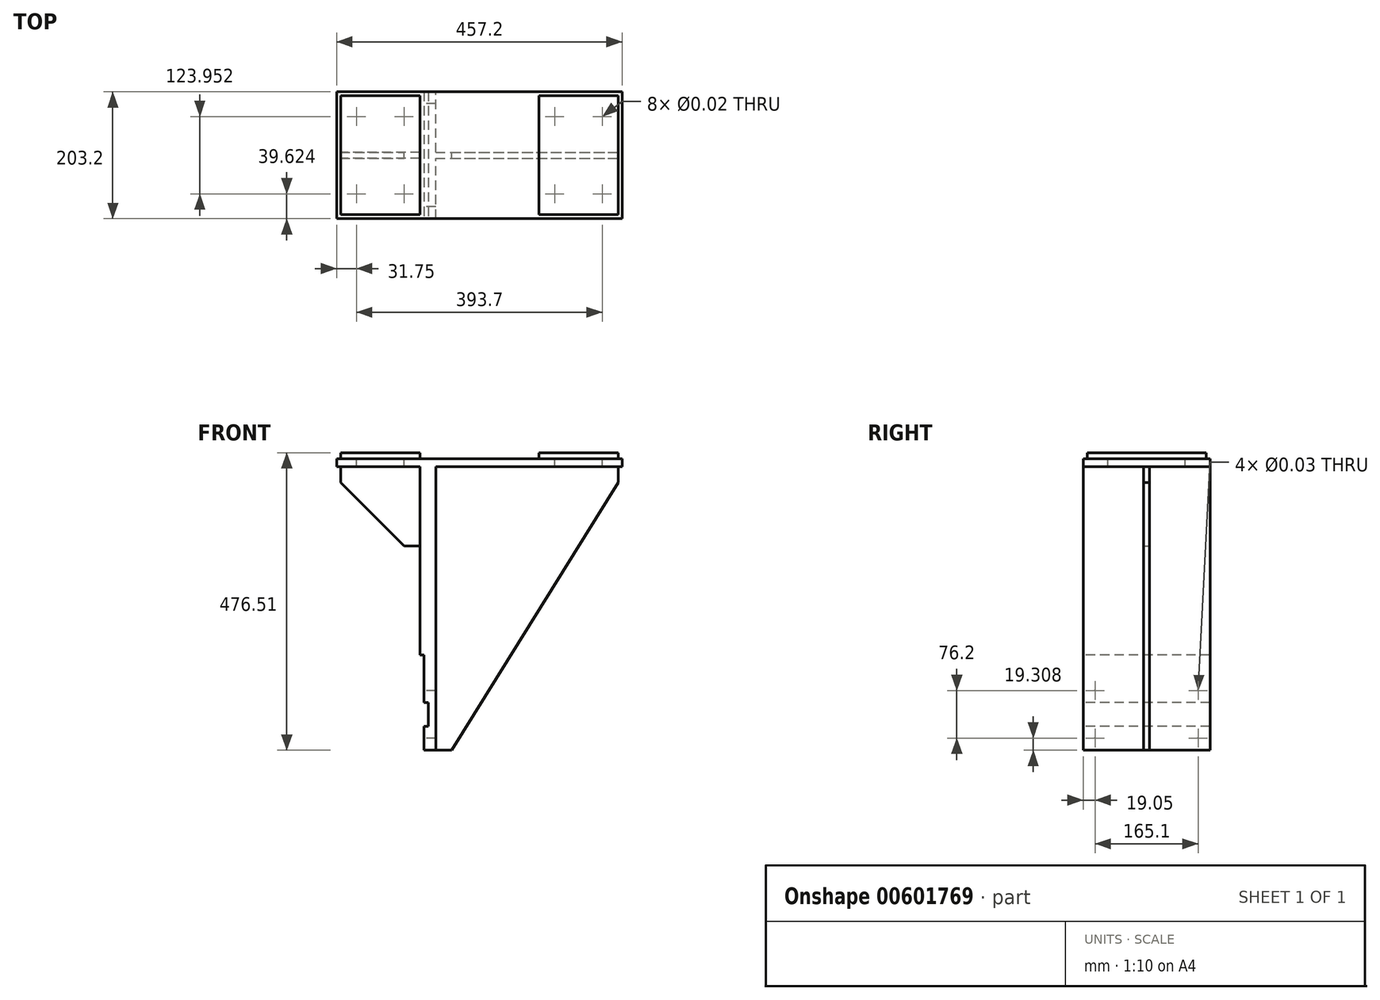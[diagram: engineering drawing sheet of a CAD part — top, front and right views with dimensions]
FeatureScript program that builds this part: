
annotation { "Feature Type Name" : "Feature", "Feature Type Description" : "" }
export const myFeature = defineFeature(function(context is Context, id is Id, definition is map)
    precondition{}
    {
        {
            var Q0;
            Q0=qCreatedBy(makeId("Right.planeOp"),FACE);
            var sketch = newSketch(context, id + "F0", { "sketchPlane" : qUnion([Q0])});
            skLineSegment(sketch, "E0.bottom", {"start": v(-101.6, 227.08) * mm, "end": v(101.6, 227.08) * mm});
            skLineSegment(sketch, "E0.top", {"start": v(-101.6, -227.08) * mm, "end": v(101.6, -227.08) * mm});
            skLineSegment(sketch, "E0.left", {"start": v(-101.6, 227.08) * mm, "end": v(-101.6, -227.08) * mm});
            skLineSegment(sketch, "E0.right", {"start": v(101.6, 227.08) * mm, "end": v(101.6, -227.08) * mm});
            skPoint(sketch, "E0.middle", {"position": v(0, 0) * mm});
            skSolve(sketch);
        }
        {
            var Q0;
            Q0=qSketchRegion(id+"F0",true);
            extrude(context, id + "F1", {"entities" : qUnion([Q0]), "depth" : 25.4 * mm, "offsetDistance" : 25.4 * mm});
        }
        {
            var Q0;
            Q0=makeQuery(id+"F1.opExtrude","SWEPT_FACE",FACE,{"disambiguationData":[OSD([sQuery(id+"F0.wireOp",EDGE,"E0.left")])]});
            var sketch = newSketch(context, id + "F2", { "sketchPlane" : qUnion([Q0])});
            skLineSegment(sketch, "E1.bottom", {"start": v(0, -227.08) * mm, "end": v(6.35, -227.08) * mm});
            skLineSegment(sketch, "E1.top", {"start": v(0, -74.68) * mm, "end": v(6.35, -74.68) * mm});
            skLineSegment(sketch, "E1.left", {"start": v(0, -227.08) * mm, "end": v(0, -74.68) * mm});
            skLineSegment(sketch, "E1.right", {"start": v(6.35, -227.08) * mm, "end": v(6.35, -74.68) * mm});
            skSolve(sketch);
        }
        {
            var Q0;
            Q0=qSketchRegion(id+"F2",true);
            extrude(context, id + "F3", {"entities" : qUnion([Q0]), "operationType" : NewBodyOperationType.REMOVE, "endBound" : BoundingType.THROUGH_ALL, "oppositeDirection" : true, "depth" : 25.4 * mm, "offsetDistance" : 25.4 * mm});
        }
        {
            var Q0;
            Q0=makeQuery(id+"F1.opExtrude","SWEPT_FACE",FACE,{"disambiguationData":[OSD([sQuery(id+"F0.wireOp",EDGE,"E0.bottom")])]});
            var sketch = newSketch(context, id + "F4", { "sketchPlane" : qUnion([Q0])});
            skLineSegment(sketch, "E2.0", {"start": v(323.85, -101.6) * mm, "end": v(323.85, 101.6) * mm});
            skLineSegment(sketch, "E3.0", {"start": v(-133.35, -101.6) * mm, "end": v(-133.35, 101.6) * mm});
            skLineSegment(sketch, "E4", {"start": v(-133.35, 101.6) * mm, "end": v(323.85, 101.6) * mm});
            skLineSegment(sketch, "E5", {"start": v(-133.35, -101.6) * mm, "end": v(323.85, -101.6) * mm});
            skSolve(sketch);
        }
        {
            var Q0;
            Q0=qSketchRegion(id+"F4",true);
            extrude(context, id + "F5", {"entities" : qUnion([Q0]), "operationType" : NewBodyOperationType.ADD, "depth" : 12.7 * mm, "offsetDistance" : 25.4 * mm});
        }
        {
            var Q0;
            Q0=makeQuery(id+"F5.opExtrude","CAP_FACE",FACE,{"disambiguationData":[OSD([sQuery(id+"F4.wireOp",EDGE,"E2.0"),sQuery(id+"F4.wireOp",EDGE,"E3.0"),sQuery(id+"F4.wireOp",EDGE,"E4"),sQuery(id+"F4.wireOp",EDGE,"E5")])],"isStart":false});
            var sketch = newSketch(context, id + "F6", { "sketchPlane" : qUnion([Q0])});
            skLineSegment(sketch, "E6.0", {"start": v(-127, -101.6) * mm, "end": v(-127, 101.6) * mm});
            skLineSegment(sketch, "E7.0", {"start": v(0, -101.6) * mm, "end": v(0, 101.6) * mm});
            skLineSegment(sketch, "E8.0", {"start": v(190.5, -101.6) * mm, "end": v(190.5, 101.6) * mm});
            skLineSegment(sketch, "E9.0", {"start": v(317.5, -101.6) * mm, "end": v(317.5, 101.6) * mm});
            skLineSegment(sketch, "E10.0", {"start": v(-133.35, -95.25) * mm, "end": v(0, -95.25) * mm});
            skLineSegment(sketch, "E11.0", {"start": v(-133.35, 95.25) * mm, "end": v(0, 95.25) * mm});
            skLineSegment(sketch, "E12.trimOffspring", {"start": v(190.5, 95.25) * mm, "end": v(323.85, 95.25) * mm});
            skLineSegment(sketch, "E13.trimOffspring", {"start": v(190.5, -95.25) * mm, "end": v(323.85, -95.25) * mm});
            skSolve(sketch);
        }
        {
            var Q0;
            Q0=qSketchRegion(id+"F6",true);
            extrude(context, id + "F7", {"entities" : qUnion([Q0]), "depth" : 9.65 * mm, "offsetDistance" : 25.4 * mm});
        }
        {
            var Q0;
            Q0=makeQuery(id+"F7.opExtrude","CAP_FACE",FACE,{"disambiguationData":[OSD([sQuery(id+"F6.wireOp",EDGE,"E8.0"),sQuery(id+"F6.wireOp",EDGE,"E9.0"),sQuery(id+"F6.wireOp",EDGE,"E12.trimOffspring"),sQuery(id+"F6.wireOp",EDGE,"E13.trimOffspring")])],"isStart":false});
            var sketch = newSketch(context, id + "F8", { "sketchPlane" : qUnion([Q0])});
            skLineSegment(sketch, "E14", {"start": v(254, 95.25) * mm, "end": v(254, -95.25) * mm, "construction": true});
            skLineSegment(sketch, "E15.0", {"start": v(-127, 95.25) * mm, "end": v(0, 95.25) * mm, "construction": true});
            skLineSegment(sketch, "E16.0", {"start": v(-127, -95.25) * mm, "end": v(0, -95.25) * mm, "construction": true});
            skLineSegment(sketch, "E17.0", {"start": v(317.5, -95.25) * mm, "end": v(317.5, 95.25) * mm, "construction": true});
            skLineSegment(sketch, "E18", {"start": v(-63.5, -95.25) * mm, "end": v(-63.5, 95.25) * mm, "construction": true});
            skLineSegment(sketch, "E19", {"start": v(317.5, 0) * mm, "end": v(-144.3, 0) * mm, "construction": true});
            skLineSegment(sketch, "E20.0", {"start": v(-25.4, -95.25) * mm, "end": v(-25.4, 95.25) * mm, "construction": true});
            skLineSegment(sketch, "E21.0", {"start": v(215.9, 95.25) * mm, "end": v(215.9, -95.25) * mm, "construction": true});
            skLineSegment(sketch, "E22.0", {"start": v(317.5, 61.98) * mm, "end": v(-144.3, 61.98) * mm, "construction": true});
            skPoint(sketch, "E23", {"position": v(-25.4, 61.98) * mm});
            skPoint(sketch, "E24", {"position": v(215.9, 61.98) * mm});
            skPoint(sketch, "E25.0.1.0", {"position": v(215.9, -61.98) * mm});
            skPoint(sketch, "E25.1.0.0", {"position": v(292.1, 61.98) * mm});
            skPoint(sketch, "E25.1.1.0", {"position": v(292.1, -61.98) * mm});
            skLineSegment(sketch, "E25.direction1", {"start": v(215.9, 61.98) * mm, "end": v(292.1, 61.98) * mm, "construction": true});
            skLineSegment(sketch, "E25.direction2", {"start": v(215.9, 61.98) * mm, "end": v(215.9, -61.98) * mm, "construction": true});
            skPoint(sketch, "E26.0.1.0", {"position": v(-25.4, -61.98) * mm});
            skPoint(sketch, "E26.1.0.0", {"position": v(-101.6, 61.98) * mm});
            skPoint(sketch, "E26.1.1.0", {"position": v(-101.6, -61.98) * mm});
            skLineSegment(sketch, "E26.direction1", {"start": v(-25.4, 61.98) * mm, "end": v(-101.6, 61.98) * mm, "construction": true});
            skLineSegment(sketch, "E26.direction2", {"start": v(-25.4, 61.98) * mm, "end": v(-25.4, -61.98) * mm, "construction": true});
            skSolve(sketch);
        }
        {
            var Q0;
            Q0=sQuery(id+"F8.wireOp",VERTEX,"E26.1.0.0");
            var Q1;
            Q1=sQuery(id+"F8.wireOp",VERTEX,"E23");
            var Q2;
            Q2=sQuery(id+"F8.wireOp",VERTEX,"E26.1.1.0");
            var Q3;
            Q3=sQuery(id+"F8.wireOp",VERTEX,"E26.0.1.0");
            var Q4;
            Q4=sQuery(id+"F8.wireOp",VERTEX,"E24");
            var Q5;
            Q5=sQuery(id+"F8.wireOp",VERTEX,"E25.1.0.0");
            var Q6;
            Q6=sQuery(id+"F8.wireOp",VERTEX,"E25.0.1.0");
            var Q7;
            Q7=sQuery(id+"F8.wireOp",VERTEX,"E25.1.1.0");
            var Q8;
            Q8=makeQuery(id+"F1.opExtrude","SWEPT_BODY",BODY,{"disambiguationData":[OSD([sQuery(id+"F0.wireOp",EDGE,"E0.bottom"),sQuery(id+"F0.wireOp",EDGE,"E0.top"),sQuery(id+"F0.wireOp",EDGE,"E0.left"),sQuery(id+"F0.wireOp",EDGE,"E0.right")])]});
            hole(context, id + "F9", {"style" : HoleStyle.SIMPLE, "endStyle" : HoleEndStyle.THROUGH, "standardTappedOrClearance" : lookupTablePath({ "standard" : "ANSI", "size" : "7/16 (0.44)", "type" : "Drilled" }), "standardBlindInLast" : lookupTablePath({ "standard" : "ANSI", "size" : "7/16", "type" : "Drilled" }), "holeDiameter" : 7 / 406.4 * mm, "majorDiameter" : 12.7 * mm, "isTappedThrough" : true, "tappedDepth" : 25.4 * mm, "tapClearance" : 3, "locations" : qUnion([Q0, Q1, Q2, Q3, Q4, Q5, Q6, Q7]), "scope" : qUnion([Q8])});
        }
        {
            var Q0;
            Q0=qCreatedBy(makeId("Front.planeOp"),FACE);
            var sketch = newSketch(context, id + "F10", { "sketchPlane" : qUnion([Q0])});
            skLineSegment(sketch, "E27.0", {"start": v(25.4, 227.08) * mm, "end": v(323.85, 227.08) * mm});
            skLineSegment(sketch, "E28.0", {"start": v(25.4, 227.08) * mm, "end": v(25.4, -227.08) * mm});
            skLineSegment(sketch, "E29.0", {"start": v(25.4, 201.68) * mm, "end": v(323.85, 201.68) * mm, "construction": true});
            skLineSegment(sketch, "E30.0", {"start": v(50.8, 227.08) * mm, "end": v(50.8, -227.08) * mm, "construction": true});
            skLineSegment(sketch, "E31", {"start": v(323.85, 227.08) * mm, "end": v(323.85, 95.77) * mm, "construction": true});
            skLineSegment(sketch, "E32.0", {"start": v(317.5, 227.08) * mm, "end": v(317.5, 201.68) * mm});
            skLineSegment(sketch, "E33", {"start": v(25.4, -227.08) * mm, "end": v(50.8, -227.08) * mm});
            skLineSegment(sketch, "E34", {"start": v(50.8, -227.08) * mm, "end": v(317.5, 201.68) * mm});
            skSolve(sketch);
        }
        {
            var Q0;
            Q0=qSketchRegion(id+"F10",true);
            extrude(context, id + "F11", {"entities" : qUnion([Q0]), "operationType" : NewBodyOperationType.ADD, "endBound" : BoundingType.SYMMETRIC, "depth" : 9.52 * mm, "offsetDistance" : 25.4 * mm});
        }
        {
            var Q0;
            Q0=makeQuery(id+"F5.boolean.opBoolean","MERGE",FACE,{"derivedFrom":[makeQuery(id+"F1.opExtrude","SWEPT_FACE",FACE,{"disambiguationData":[OSD([sQuery(id+"F0.wireOp",EDGE,"E0.left")])]}),makeQuery(id+"F5.opExtrude","SWEPT_FACE",FACE,{"disambiguationData":[OSD([sQuery(id+"F4.wireOp",EDGE,"E5")])]})]});
            var sketch = newSketch(context, id + "F12", { "sketchPlane" : qUnion([Q0])});
            skLineSegment(sketch, "E35.0", {"start": v(-127, 249.43) * mm, "end": v(0, 249.43) * mm, "construction": true});
            skLineSegment(sketch, "E36.0", {"start": v(-127, -169.67) * mm, "end": v(0, -169.67) * mm, "construction": true});
            skLineSegment(sketch, "E37.0", {"start": v(-127, -188.72) * mm, "end": v(13.2, -188.72) * mm, "construction": true});
            skLineSegment(sketch, "E38.0", {"start": v(13.2, -227.08) * mm, "end": v(13.2, -74.68) * mm, "construction": true});
            skLineSegment(sketch, "E39.bottom", {"start": v(13.2, -188.72) * mm, "end": v(-24.9, -188.72) * mm});
            skLineSegment(sketch, "E39.top", {"start": v(13.2, -150.62) * mm, "end": v(-24.9, -150.62) * mm});
            skLineSegment(sketch, "E39.left", {"start": v(13.2, -188.72) * mm, "end": v(13.2, -150.62) * mm});
            skLineSegment(sketch, "E39.right", {"start": v(-24.9, -188.72) * mm, "end": v(-24.9, -150.62) * mm});
            skSolve(sketch);
        }
        {
            var Q0;
            Q0=qSketchRegion(id+"F12",true);
            extrude(context, id + "F13", {"entities" : qUnion([Q0]), "operationType" : NewBodyOperationType.REMOVE, "endBound" : BoundingType.THROUGH_ALL, "oppositeDirection" : true, "depth" : 25.4 * mm, "offsetDistance" : 25.4 * mm});
        }
        {
            var Q0;
            Q0=makeQuery(id+"F13.boolean.opBoolean","SPLIT",FACE,{"disambiguationData":[TD([makeQuery(id+"F3.boolean.opBoolean","COPY",FACE,{"derivedFrom":makeQuery(id+"F3.opExtrude","SWEPT_FACE",FACE,{"disambiguationData":[OSD([sQuery(id+"F2.wireOp",EDGE,"E1.top")])]})})])],"derivedFrom":makeQuery(id+"F3.boolean.opBoolean","COPY",FACE,{"derivedFrom":makeQuery(id+"F3.opExtrude","SWEPT_FACE",FACE,{"disambiguationData":[OSD([sQuery(id+"F2.wireOp",EDGE,"E1.right")])]})})});
            var sketch = newSketch(context, id + "F14", { "sketchPlane" : qUnion([Q0])});
            skLineSegment(sketch, "E40.0", {"start": v(95.25, -169.67) * mm, "end": v(-95.25, -169.67) * mm, "construction": true});
            skLineSegment(sketch, "E41.0", {"start": v(95.25, -207.77) * mm, "end": v(-95.25, -207.77) * mm, "construction": true});
            skLineSegment(sketch, "E42", {"start": v(0, 289.27) * mm, "end": v(0, -288.68) * mm, "construction": true});
            skPoint(sketch, "E42.endSnap0", {"position": v(0, -207.77) * mm});
            skLineSegment(sketch, "E43.0", {"start": v(-82.55, 289.27) * mm, "end": v(-82.55, -288.68) * mm, "construction": true});
            skPoint(sketch, "E44", {"position": v(-82.55, -207.77) * mm});
            skPoint(sketch, "E45.0.1.0", {"position": v(-82.55, -131.57) * mm});
            skPoint(sketch, "E45.1.0.0", {"position": v(82.55, -207.77) * mm});
            skPoint(sketch, "E45.1.1.0", {"position": v(82.55, -131.57) * mm});
            skLineSegment(sketch, "E45.direction1", {"start": v(-82.55, -207.77) * mm, "end": v(82.55, -207.77) * mm, "construction": true});
            skLineSegment(sketch, "E45.direction2", {"start": v(-82.55, -207.77) * mm, "end": v(-82.55, -131.57) * mm, "construction": true});
            skSolve(sketch);
        }
        {
            var Q0;
            Q0=sQuery(id+"F14.wireOp",VERTEX,"E45.0.1.0");
            var Q1;
            Q1=sQuery(id+"F14.wireOp",VERTEX,"E45.1.1.0");
            var Q2;
            Q2=sQuery(id+"F14.wireOp",VERTEX,"E45.1.0.0");
            var Q3;
            Q3=sQuery(id+"F14.wireOp",VERTEX,"E44");
            var Q4;
            Q4=makeQuery(id+"F1.opExtrude","SWEPT_BODY",BODY,{"disambiguationData":[OSD([sQuery(id+"F0.wireOp",EDGE,"E0.bottom"),sQuery(id+"F0.wireOp",EDGE,"E0.top"),sQuery(id+"F0.wireOp",EDGE,"E0.left"),sQuery(id+"F0.wireOp",EDGE,"E0.right")])]});
            hole(context, id + "F15", {"style" : HoleStyle.SIMPLE, "endStyle" : HoleEndStyle.THROUGH, "standardTappedOrClearance" : lookupTablePath({ "standard" : "ANSI", "size" : "11/16 (0.69)", "type" : "Drilled" }), "standardBlindInLast" : lookupTablePath({ "standard" : "ANSI", "size" : "11/16", "type" : "Drilled" }), "holeDiameter" : 11 / 406.4 * mm, "majorDiameter" : 6.35 * mm, "isTappedThrough" : true, "tappedDepth" : 25.4 * mm, "tapClearance" : 3, "locations" : qUnion([Q0, Q1, Q2, Q3]), "scope" : qUnion([Q4])});
        }
        {
            var Q0;
            Q0=qCreatedBy(makeId("Front.planeOp"),FACE);
            var sketch = newSketch(context, id + "F16", { "sketchPlane" : qUnion([Q0])});
            skLineSegment(sketch, "E46.0", {"start": v(-133.35, 227.08) * mm, "end": v(0, 227.08) * mm, "construction": true});
            skLineSegment(sketch, "E47.bottom", {"start": v(0, 227.08) * mm, "end": v(-127, 227.08) * mm});
            skLineSegment(sketch, "E47.top", {"start": v(0, 100.08) * mm, "end": v(-127, 100.08) * mm});
            skLineSegment(sketch, "E47.left", {"start": v(0, 227.08) * mm, "end": v(0, 100.08) * mm});
            skLineSegment(sketch, "E47.right", {"start": v(-127, 227.08) * mm, "end": v(-127, 201.68) * mm});
            skLineSegment(sketch, "E48.bottom", {"start": v(-127, 100.08) * mm, "end": v(-25.4, 100.08) * mm, "construction": true});
            skLineSegment(sketch, "E48.top", {"start": v(-127, 201.68) * mm, "end": v(-25.4, 201.68) * mm, "construction": true});
            skLineSegment(sketch, "E48.right", {"start": v(-25.4, 100.08) * mm, "end": v(-25.4, 201.68) * mm, "construction": true});
            skLineSegment(sketch, "E49", {"start": v(-127, 201.68) * mm, "end": v(-25.4, 100.08) * mm});
            skSolve(sketch);
        }
        {
            var Q0;
            Q0=qSketchRegion(id+"F16",true);
            extrude(context, id + "F17", {"entities" : qUnion([Q0]), "operationType" : NewBodyOperationType.ADD, "endBound" : BoundingType.SYMMETRIC, "depth" : 9.65 * mm, "offsetDistance" : 25.4 * mm});
        }
    });
